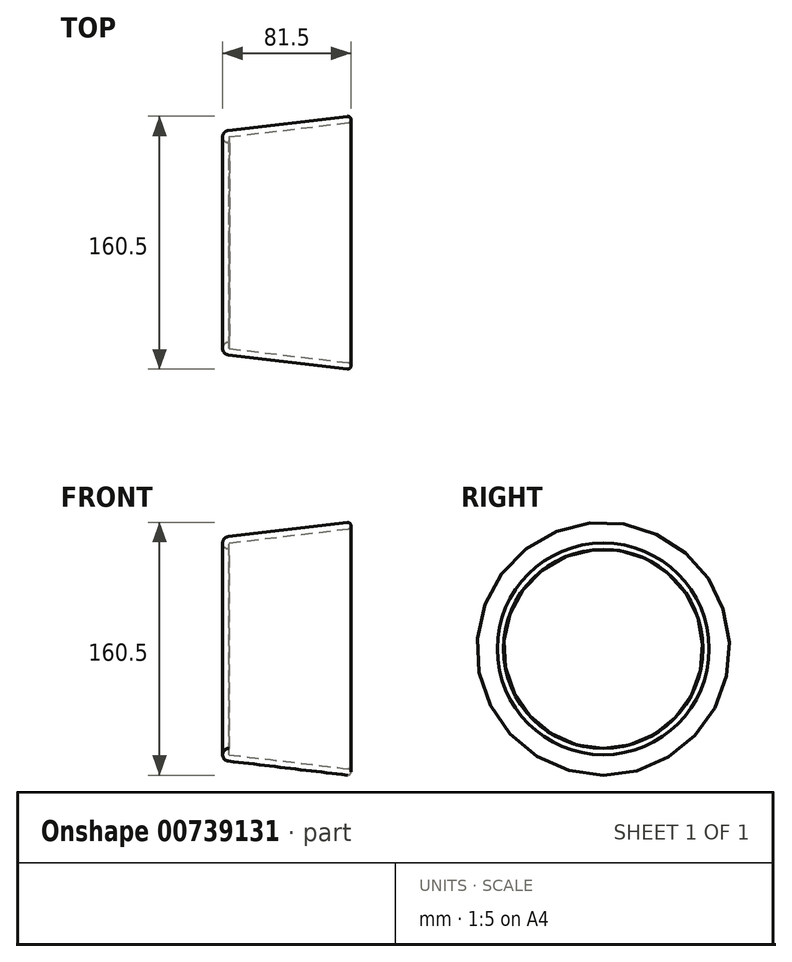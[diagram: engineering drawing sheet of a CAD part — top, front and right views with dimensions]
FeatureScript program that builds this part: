
annotation { "Feature Type Name" : "Feature", "Feature Type Description" : "" }
export const myFeature = defineFeature(function(context is Context, id is Id, definition is map)
    precondition{}
    {
        {
            var Q0;
            Q0=qCreatedBy(makeId("Top.planeOp"),FACE);
            var sketch = newSketch(context, id + "F0", { "sketchPlane" : qUnion([Q0])});
            skLineSegment(sketch, "E0", {"start": v(0, 0) * mm, "end": v(-75.67, 8.96) * mm});
            skLineSegment(sketch, "E1", {"start": v(-0.48, -4.04) * mm, "end": v(-76.15, 4.92) * mm});
            skArc(sketch, "E2", {"start": v(0, 0) * mm, "mid": v(1.78, -2.26) * mm, "end": v(-0.48, -4.04) * mm});
            skArc(sketch, "E3", {"start": v(-76.15, 4.92) * mm, "mid": v(-79.69, 9.4) * mm, "end": v(-75.2, 12.94) * mm});
            skLineSegment(sketch, "E4", {"start": v(-76.15, 4.92) * mm, "end": v(-75.2, 12.94) * mm, "construction": true});
            skLineSegment(sketch, "E5", {"start": v(-75.32, 76.2) * mm, "end": v(48.94, 76.2) * mm, "construction": true});
            skSolve(sketch);
        }
        {
            var Q0;
            Q0 = qSketchRegion(id + "F0", true);
            var Q1;
            Q1=sQuery(id+"F0.wireOp",EDGE,"E1");
            var Q2;
            Q2=sQuery(id+"F0.wireOp",EDGE,"E3");
            var Q3;
            Q3=sQuery(id+"F0.wireOp",EDGE,"E0");
            var Q4;
            Q4=sQuery(id+"F0.wireOp",EDGE,"E2");
            var Q5;
            Q5=sQuery(id+"F0.wireOp",EDGE,"E5");
            revolve(context, id + "F1", {"bodyType" : ToolBodyType.SURFACE, "surfaceOperationType" : NewSurfaceOperationType.NEW, "entities" : qUnion([Q0]), "surfaceEntities" : qUnion([Q1, Q2, Q3, Q4]), "axis" : qUnion([Q5]), "revolveType" : RevolveType.FULL});
        }
    });
